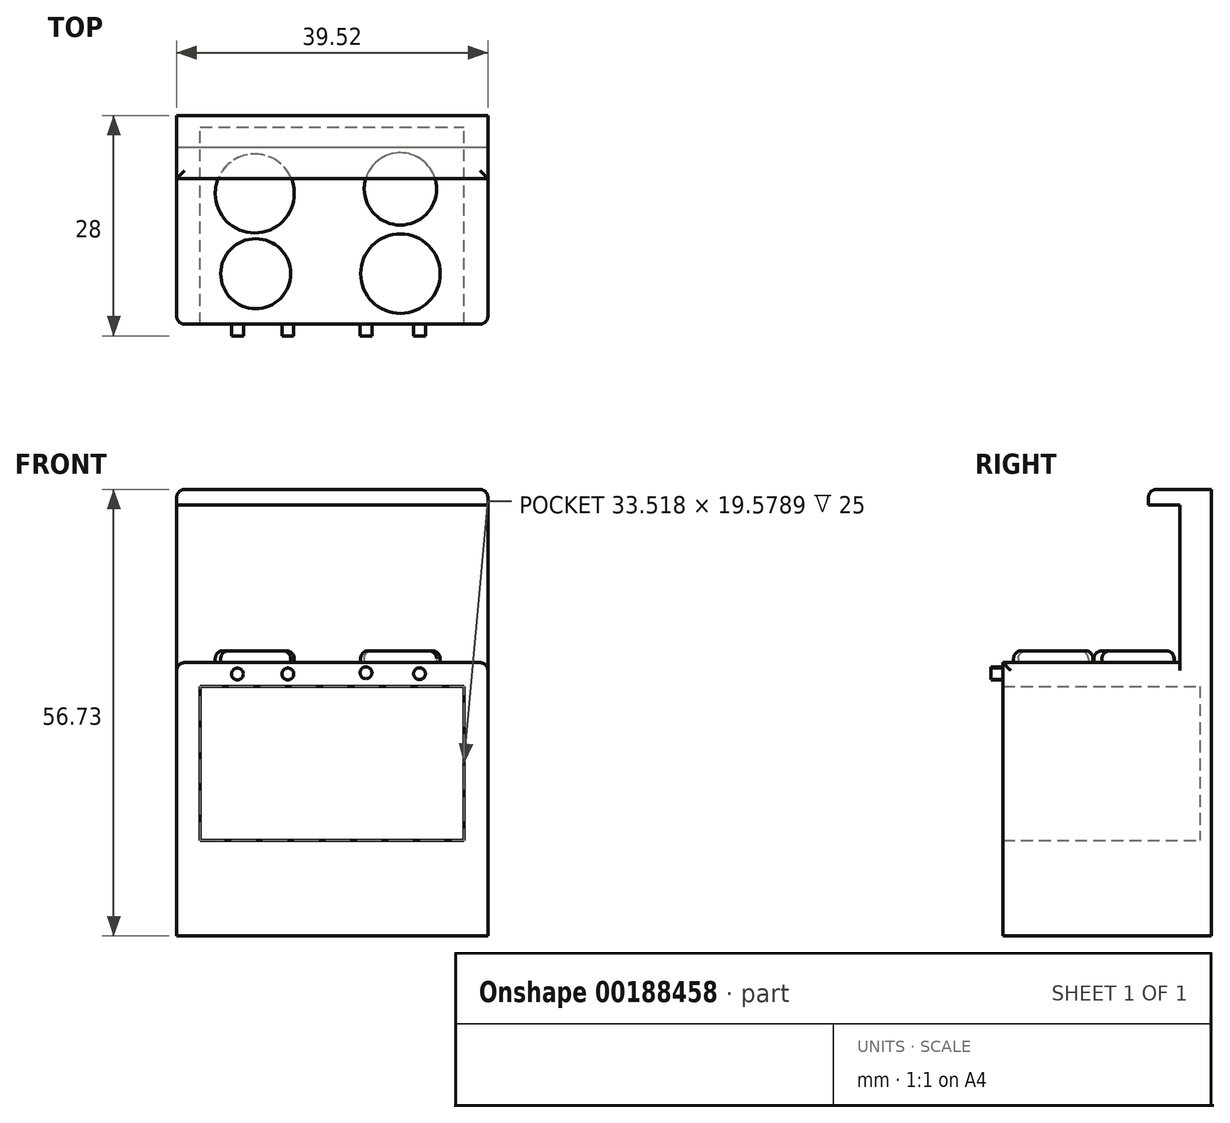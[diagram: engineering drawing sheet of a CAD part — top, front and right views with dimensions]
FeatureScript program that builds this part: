
annotation { "Feature Type Name" : "Feature", "Feature Type Description" : "" }
export const myFeature = defineFeature(function(context is Context, id is Id, definition is map)
    precondition{}
    {
        {
            var Q0;
            Q0=qCreatedBy(makeId("Front.planeOp"),FACE);
            var sketch = newSketch(context, id + "F0", { "sketchPlane" : qUnion([Q0])});
            skLineSegment(sketch, "E0.bottom", {"start": v(19.76, -17.36) * mm, "end": v(-19.76, -17.36) * mm});
            skLineSegment(sketch, "E0.top", {"start": v(19.76, 17.36) * mm, "end": v(-19.76, 17.36) * mm});
            skLineSegment(sketch, "E0.left", {"start": v(19.76, -17.36) * mm, "end": v(19.76, 17.36) * mm});
            skLineSegment(sketch, "E0.right", {"start": v(-19.76, -17.36) * mm, "end": v(-19.76, 17.36) * mm});
            skPoint(sketch, "E0.middle", {"position": v(0, 0) * mm});
            skLineSegment(sketch, "E1.bottom", {"start": v(-16.76, 14.36) * mm, "end": v(16.76, 14.36) * mm});
            skLineSegment(sketch, "E1.top", {"start": v(-16.76, -5.22) * mm, "end": v(16.76, -5.22) * mm});
            skLineSegment(sketch, "E1.left", {"start": v(-16.76, 14.36) * mm, "end": v(-16.76, -5.22) * mm});
            skLineSegment(sketch, "E1.right", {"start": v(16.76, 14.36) * mm, "end": v(16.76, -5.22) * mm});
            skPoint(sketch, "E2.first.point", {"position": v(-17.08, -12.07) * mm});
            skPoint(sketch, "E2.second.point", {"position": v(-13.87, -12.16) * mm});
            skPoint(sketch, "E2.third.point", {"position": v(-13.95, -14.63) * mm});
            skPoint(sketch, "E3.first.point", {"position": v(-1.68, -12.24) * mm});
            skPoint(sketch, "E3.second.point", {"position": v(1.7, -14.46) * mm});
            skPoint(sketch, "E3.third.point", {"position": v(0, -15.2) * mm});
            skPoint(sketch, "E4.first.point", {"position": v(15.2, -15.2) * mm});
            skPoint(sketch, "E4.second.point", {"position": v(17.18, -13.72) * mm});
            skPoint(sketch, "E4.third.point", {"position": v(14.3, -11.17) * mm});
            skSolve(sketch);
        }
        {
            var Q0;
            Q0=makeQuery(id+"F0.imprint","IMPRINT",FACE,{"disambiguationData":[TD([[makeQuery(id+"F0.imprint","IMPRINT",EDGE,{"derivedFrom":sQuery(id+"F0.wireOp",EDGE,"E0.bottom")}),-1.0]])]});
            extrude(context, id + "F1", {"entities" : qUnion([Q0]), "depth" : 25 * mm});
        }
        {
            var Q0;
            Q0=makeQuery(id+"F1.opExtrude","SWEPT_FACE",FACE,{"disambiguationData":[OSD([sQuery(id+"F0.wireOp",EDGE,"E0.top")])]});
            var sketch = newSketch(context, id + "F2", { "sketchPlane" : qUnion([Q0])});
            skLineSegment(sketch, "E5.bottom", {"start": v(-19.76, 0) * mm, "end": v(19.76, 0) * mm});
            skLineSegment(sketch, "E5.top", {"start": v(-19.76, -2.5) * mm, "end": v(19.76, -2.5) * mm});
            skLineSegment(sketch, "E5.left", {"start": v(-19.76, 0) * mm, "end": v(-19.76, -2.5) * mm});
            skLineSegment(sketch, "E5.right", {"start": v(19.76, 0) * mm, "end": v(19.76, -2.5) * mm});
            skLineSegment(sketch, "E6.bottom", {"start": v(19.76, -2.5) * mm, "end": v(17.76, -2.5) * mm});
            skLineSegment(sketch, "E6.top", {"start": v(19.76, -6.5) * mm, "end": v(17.76, -6.5) * mm});
            skLineSegment(sketch, "E6.left", {"start": v(19.76, -2.5) * mm, "end": v(19.76, -6.5) * mm});
            skLineSegment(sketch, "E6.right", {"start": v(17.76, -2.5) * mm, "end": v(17.76, -6.5) * mm});
            skLineSegment(sketch, "E7.bottom", {"start": v(-19.76, -2.5) * mm, "end": v(-17.76, -2.5) * mm});
            skLineSegment(sketch, "E7.top", {"start": v(-19.76, -6.5) * mm, "end": v(-17.76, -6.5) * mm});
            skLineSegment(sketch, "E7.left", {"start": v(-19.76, -2.5) * mm, "end": v(-19.76, -6.5) * mm});
            skLineSegment(sketch, "E7.right", {"start": v(-17.76, -2.5) * mm, "end": v(-17.76, -6.5) * mm});
            skCircle(sketch, "E8", {"center": v(-9.85, -8.4) * mm, "radius": 5.02 * mm});
            skCircle(sketch, "E9", {"center": v(-9.73, -18.59) * mm, "radius": 4.44 * mm});
            skCircle(sketch, "E10", {"center": v(8.65, -7.82) * mm, "radius": 4.6 * mm});
            skCircle(sketch, "E11", {"center": v(8.65, -18.59) * mm, "radius": 5.05 * mm});
            skSolve(sketch);
        }
        {
            var Q0;
            Q0=makeQuery(id+"F2.imprint","IMPRINT",FACE,{"disambiguationData":[TD([[makeQuery(id+"F2.imprint","IMPRINT",EDGE,{"derivedFrom":sQuery(id+"F2.wireOp",EDGE,"E7.bottom")}),-1.0]])]});
            var Q1;
            Q1=makeQuery(id+"F2.imprint","IMPRINT",FACE,{"disambiguationData":[TD([[makeQuery(id+"F2.imprint","IMPRINT",EDGE,{"derivedFrom":sQuery(id+"F2.wireOp",EDGE,"E5.bottom")}),1.0]])]});
            var Q2;
            Q2=makeQuery(id+"F2.imprint","IMPRINT",FACE,{"disambiguationData":[TD([[makeQuery(id+"F2.imprint","IMPRINT",EDGE,{"derivedFrom":sQuery(id+"F2.wireOp",EDGE,"E6.bottom")}),1.0]])]});
            extrude(context, id + "F3", {"entities" : qUnion([Q0, Q1, Q2]), "operationType" : NewBodyOperationType.ADD, "depth" : 20 * mm});
        }
        {
            var Q0;
            Q0=makeQuery(id+"F3.opExtrude","CAP_FACE",FACE,{"disambiguationData":[OSD([sQuery(id+"F2.wireOp",EDGE,"E5.bottom"),sQuery(id+"F2.wireOp",EDGE,"E5.top"),sQuery(id+"F2.wireOp",EDGE,"E5.left"),sQuery(id+"F2.wireOp",EDGE,"E5.right"),sQuery(id+"F2.wireOp",EDGE,"E6.top"),sQuery(id+"F2.wireOp",EDGE,"E6.left"),sQuery(id+"F2.wireOp",EDGE,"E6.right"),sQuery(id+"F2.wireOp",EDGE,"E7.top"),sQuery(id+"F2.wireOp",EDGE,"E7.left"),sQuery(id+"F2.wireOp",EDGE,"E7.right")])],"isStart":false});
            var sketch = newSketch(context, id + "F4", { "sketchPlane" : qUnion([Q0])});
            skLineSegment(sketch, "E12.bottom", {"start": v(-19.76, 0) * mm, "end": v(19.76, 0) * mm});
            skLineSegment(sketch, "E12.top", {"start": v(-19.76, -6.5) * mm, "end": v(19.76, -6.5) * mm});
            skLineSegment(sketch, "E12.left", {"start": v(-19.76, 0) * mm, "end": v(-19.76, -6.5) * mm});
            skLineSegment(sketch, "E12.right", {"start": v(19.76, 0) * mm, "end": v(19.76, -6.5) * mm});
            skSolve(sketch);
        }
        {
            var Q0;
            Q0=makeQuery(id+"F4.imprint","IMPRINT",FACE,{"disambiguationData":[TD([[makeQuery(id+"F4.imprint","IMPRINT",EDGE,{"derivedFrom":makeQuery(id+"F3.opExtrude","CAP_EDGE",EDGE,{"disambiguationData":[OSD([sQuery(id+"F2.wireOp",EDGE,"E5.top")])],"isStart":false})}),-1.0]])]});
            var Q1;
            Q1=makeQuery(id+"F4.imprint","IMPRINT",FACE,{"disambiguationData":[TD([[makeQuery(id+"F4.imprint","IMPRINT",EDGE,{"derivedFrom":sQuery(id+"F4.wireOp",EDGE,"E12.bottom")}),1.0]])]});
            extrude(context, id + "F5", {"entities" : qUnion([Q0, Q1]), "operationType" : NewBodyOperationType.ADD, "depth" : 2 * mm});
        }
        {
            var Q0;
            Q0=makeQuery(id+"F2.imprint","IMPRINT",FACE,{"disambiguationData":[TD([[makeQuery(id+"F2.imprint","IMPRINT",EDGE,{"derivedFrom":sQuery(id+"F2.wireOp",EDGE,"E8")}),1.0]])]});
            var Q1;
            Q1=makeQuery(id+"F2.imprint","IMPRINT",FACE,{"disambiguationData":[TD([[makeQuery(id+"F2.imprint","IMPRINT",EDGE,{"derivedFrom":sQuery(id+"F2.wireOp",EDGE,"E10")}),1.0]])]});
            var Q2;
            Q2=makeQuery(id+"F2.imprint","IMPRINT",FACE,{"disambiguationData":[TD([[makeQuery(id+"F2.imprint","IMPRINT",EDGE,{"derivedFrom":sQuery(id+"F2.wireOp",EDGE,"E11")}),1.0]])]});
            var Q3;
            Q3=makeQuery(id+"F2.imprint","IMPRINT",FACE,{"disambiguationData":[TD([[makeQuery(id+"F2.imprint","IMPRINT",EDGE,{"derivedFrom":sQuery(id+"F2.wireOp",EDGE,"E9")}),1.0]])]});
            extrude(context, id + "F6", {"entities" : qUnion([Q0, Q1, Q2, Q3]), "operationType" : NewBodyOperationType.ADD, "depth" : 1.5 * mm});
        }
        {
            var Q0;
            Q0=makeQuery(id+"F5.boolean.opBoolean","MERGE",FACE,{"derivedFrom":[makeQuery(id+"F3.boolean.opBoolean","MERGE",FACE,{"derivedFrom":[makeQuery(id+"F1.opExtrude","CAP_FACE",FACE,{"disambiguationData":[OSD([sQuery(id+"F0.wireOp",EDGE,"E0.bottom"),sQuery(id+"F0.wireOp",EDGE,"E0.top"),sQuery(id+"F0.wireOp",EDGE,"E0.left"),sQuery(id+"F0.wireOp",EDGE,"E0.right"),sQuery(id+"F0.wireOp",EDGE,"E1.bottom"),sQuery(id+"F0.wireOp",EDGE,"E1.top"),sQuery(id+"F0.wireOp",EDGE,"E1.left"),sQuery(id+"F0.wireOp",EDGE,"E1.right"),sQuery(id+"F0.wireOp",EDGE,"E2"),sQuery(id+"F0.wireOp",EDGE,"E3"),sQuery(id+"F0.wireOp",EDGE,"E4")])],"isStart":true}),makeQuery(id+"F3.opExtrude","SWEPT_FACE",FACE,{"disambiguationData":[OSD([sQuery(id+"F2.wireOp",EDGE,"E5.bottom")])]})]}),makeQuery(id+"F5.opExtrude","SWEPT_FACE",FACE,{"disambiguationData":[OSD([sQuery(id+"F4.wireOp",EDGE,"E12.bottom")])]})]});
            var sketch = newSketch(context, id + "F7", { "sketchPlane" : qUnion([Q0])});
            skLineSegment(sketch, "E13.bottom", {"start": v(-19.76, 39.36) * mm, "end": v(19.76, 39.36) * mm});
            skLineSegment(sketch, "E13.top", {"start": v(-19.76, -17.36) * mm, "end": v(19.76, -17.36) * mm});
            skLineSegment(sketch, "E13.left", {"start": v(-19.76, 39.36) * mm, "end": v(-19.76, -17.36) * mm});
            skLineSegment(sketch, "E13.right", {"start": v(19.76, 39.36) * mm, "end": v(19.76, -17.36) * mm});
            skLineSegment(sketch, "E14.top", {"start": v(-19.76, 34.37) * mm, "end": v(19.76, 34.37) * mm});
            skLineSegment(sketch, "E14.left", {"start": v(-19.76, 39.36) * mm, "end": v(-19.76, 34.37) * mm});
            skLineSegment(sketch, "E14.right", {"start": v(19.76, 39.36) * mm, "end": v(19.76, 34.37) * mm});
            skSolve(sketch);
        }
        {
            var Q0;
            Q0=makeQuery(id+"F7.imprint","IMPRINT",FACE,{"disambiguationData":[TD([[makeQuery(id+"F7.imprint","IMPRINT",EDGE,{"derivedFrom":sQuery(id+"F7.wireOp",EDGE,"E13.bottom")}),-1.0]])]});
            extrude(context, id + "F8", {"entities" : qUnion([Q0]), "operationType" : NewBodyOperationType.ADD, "depth" : 1.5 * mm});
        }
        {
            var Q0;
            Q0=makeQuery(id+"F8.opExtrude","SWEPT_FACE",FACE,{"disambiguationData":[OSD([sQuery(id+"F7.wireOp",EDGE,"E14.top")])]});
            extrude(context, id + "F9", {"entities" : qUnion([Q0]), "operationType" : NewBodyOperationType.ADD, "depth" : 51.74 * mm});
        }
        {
            var Q0;
            Q0=makeQuery(id+"F1.opExtrude","CAP_FACE",FACE,{"disambiguationData":[OSD([sQuery(id+"F0.wireOp",EDGE,"E0.bottom"),sQuery(id+"F0.wireOp",EDGE,"E0.top"),sQuery(id+"F0.wireOp",EDGE,"E0.left"),sQuery(id+"F0.wireOp",EDGE,"E0.right"),sQuery(id+"F0.wireOp",EDGE,"E1.bottom"),sQuery(id+"F0.wireOp",EDGE,"E1.top"),sQuery(id+"F0.wireOp",EDGE,"E1.left"),sQuery(id+"F0.wireOp",EDGE,"E1.right")])],"isStart":false});
            var sketch = newSketch(context, id + "F10", { "sketchPlane" : qUnion([Q0])});
            skCircle(sketch, "E15", {"center": v(-12.05, 15.9) * mm, "radius": 0.75 * mm});
            skCircle(sketch, "E16", {"center": v(-5.64, 15.91) * mm, "radius": 0.75 * mm});
            skCircle(sketch, "E17", {"center": v(11.08, 15.94) * mm, "radius": 0.75 * mm});
            skCircle(sketch, "E18", {"center": v(4.28, 16.06) * mm, "radius": 0.75 * mm});
            skSolve(sketch);
        }
        {
            var Q0;
            Q0=makeQuery(id+"F10.imprint","IMPRINT",FACE,{"disambiguationData":[TD([[makeQuery(id+"F10.imprint","IMPRINT",EDGE,{"derivedFrom":sQuery(id+"F10.wireOp",EDGE,"E15")}),1.0]])]});
            var Q1;
            Q1=makeQuery(id+"F10.imprint","IMPRINT",FACE,{"disambiguationData":[TD([[makeQuery(id+"F10.imprint","IMPRINT",EDGE,{"derivedFrom":sQuery(id+"F10.wireOp",EDGE,"E16")}),1.0]])]});
            var Q2;
            Q2=makeQuery(id+"F10.imprint","IMPRINT",FACE,{"disambiguationData":[TD([[makeQuery(id+"F10.imprint","IMPRINT",EDGE,{"derivedFrom":sQuery(id+"F10.wireOp",EDGE,"E18")}),1.0]])]});
            var Q3;
            Q3=makeQuery(id+"F10.imprint","IMPRINT",FACE,{"disambiguationData":[TD([[makeQuery(id+"F10.imprint","IMPRINT",EDGE,{"derivedFrom":sQuery(id+"F10.wireOp",EDGE,"E17")}),1.0]])]});
            extrude(context, id + "F11", {"entities" : qUnion([Q0, Q1, Q2, Q3]), "operationType" : NewBodyOperationType.ADD, "depth" : 1.5 * mm});
        }
        {
            var Q0;
            Q0=makeQuery(id+"F8.boolean.opBoolean","MERGE",EDGE,{"derivedFrom":[makeQuery(id+"F5.opExtrude","CAP_EDGE",EDGE,{"disambiguationData":[OSD([sQuery(id+"F4.wireOp",EDGE,"E12.right")])],"isStart":false}),makeQuery(id+"F8.opExtrude","SWEPT_EDGE",EDGE,{"disambiguationData":[OSD([sQuery(id+"F7.wireOp",EDGE,"E13.bottom"),sQuery(id+"F7.wireOp",EDGE,"E14.left")])]})]});
            var Q1;
            Q1=makeQuery(id+"F5.boolean.opBoolean","MERGE",EDGE,{"derivedFrom":[makeQuery(id+"F3.opExtrude","SWEPT_EDGE",EDGE,{"disambiguationData":[OSD([sQuery(id+"F0.wireOp",EDGE,"E0.top"),sQuery(id+"F0.wireOp",EDGE,"E0.left"),sQuery(id+"F2.wireOp",EDGE,"E6.top"),sQuery(id+"F2.wireOp",EDGE,"E6.left")])]}),makeQuery(id+"F5.opExtrude","SWEPT_EDGE",EDGE,{"disambiguationData":[OSD([sQuery(id+"F4.wireOp",EDGE,"E12.top"),sQuery(id+"F4.wireOp",EDGE,"E12.right")])]})]});
            var Q2;
            Q2=makeQuery(id+"F1.opExtrude","SWEPT_EDGE",EDGE,{"disambiguationData":[OSD([sQuery(id+"F0.wireOp",EDGE,"E0.top"),sQuery(id+"F0.wireOp",EDGE,"E0.left")])]});
            var Q3;
            Q3=makeQuery(id+"F5.opExtrude","CAP_EDGE",EDGE,{"disambiguationData":[OSD([sQuery(id+"F4.wireOp",EDGE,"E12.top")])],"isStart":false});
            var Q4;
            Q4=makeQuery(id+"F5.boolean.opBoolean","MERGE",EDGE,{"derivedFrom":[makeQuery(id+"F3.opExtrude","SWEPT_EDGE",EDGE,{"disambiguationData":[OSD([sQuery(id+"F0.wireOp",EDGE,"E0.top"),sQuery(id+"F0.wireOp",EDGE,"E0.right"),sQuery(id+"F2.wireOp",EDGE,"E7.top"),sQuery(id+"F2.wireOp",EDGE,"E7.left")])]}),makeQuery(id+"F5.opExtrude","SWEPT_EDGE",EDGE,{"disambiguationData":[OSD([sQuery(id+"F4.wireOp",EDGE,"E12.top"),sQuery(id+"F4.wireOp",EDGE,"E12.left")])]})]});
            var Q5;
            Q5=makeQuery(id+"F1.opExtrude","SWEPT_EDGE",EDGE,{"disambiguationData":[OSD([sQuery(id+"F0.wireOp",EDGE,"E0.top"),sQuery(id+"F0.wireOp",EDGE,"E0.right")])]});
            var Q6;
            Q6=makeQuery(id+"F1.opExtrude","CAP_EDGE",EDGE,{"disambiguationData":[OSD([sQuery(id+"F0.wireOp",EDGE,"E0.right")])],"isStart":false});
            var Q7;
            Q7=makeQuery(id+"F1.opExtrude","CAP_EDGE",EDGE,{"disambiguationData":[OSD([sQuery(id+"F0.wireOp",EDGE,"E0.left")])],"isStart":false});
            var Q8;
            Q8=makeQuery(id+"F6.opExtrude","CAP_EDGE",EDGE,{"disambiguationData":[OSD([sQuery(id+"F2.wireOp",EDGE,"E11")])],"isStart":false});
            var Q9;
            Q9=makeQuery(id+"F6.opExtrude","CAP_EDGE",EDGE,{"disambiguationData":[OSD([sQuery(id+"F2.wireOp",EDGE,"E10")])],"isStart":false});
            var Q10;
            Q10=makeQuery(id+"F6.opExtrude","CAP_EDGE",EDGE,{"disambiguationData":[OSD([sQuery(id+"F2.wireOp",EDGE,"E8")])],"isStart":false});
            var Q11;
            Q11=makeQuery(id+"F6.opExtrude","CAP_EDGE",EDGE,{"disambiguationData":[OSD([sQuery(id+"F2.wireOp",EDGE,"E9")])],"isStart":false});
            var Q12;
            Q12=makeQuery(id+"F8.boolean.opBoolean","MERGE",EDGE,{"derivedFrom":[makeQuery(id+"F5.opExtrude","CAP_EDGE",EDGE,{"disambiguationData":[OSD([sQuery(id+"F4.wireOp",EDGE,"E12.left")])],"isStart":false}),makeQuery(id+"F8.opExtrude","SWEPT_EDGE",EDGE,{"disambiguationData":[OSD([sQuery(id+"F7.wireOp",EDGE,"E13.bottom"),sQuery(id+"F7.wireOp",EDGE,"E14.right")])]})]});
            fillet(context, id + "F12", {"entities" : qUnion([Q0, Q1, Q2, Q3, Q4, Q5, Q6, Q7, Q8, Q9, Q10, Q11, Q12]), "radius" : 1 * mm, "tangentPropagation" : true, "allowEdgeOverflow" : false});
        }
    });
